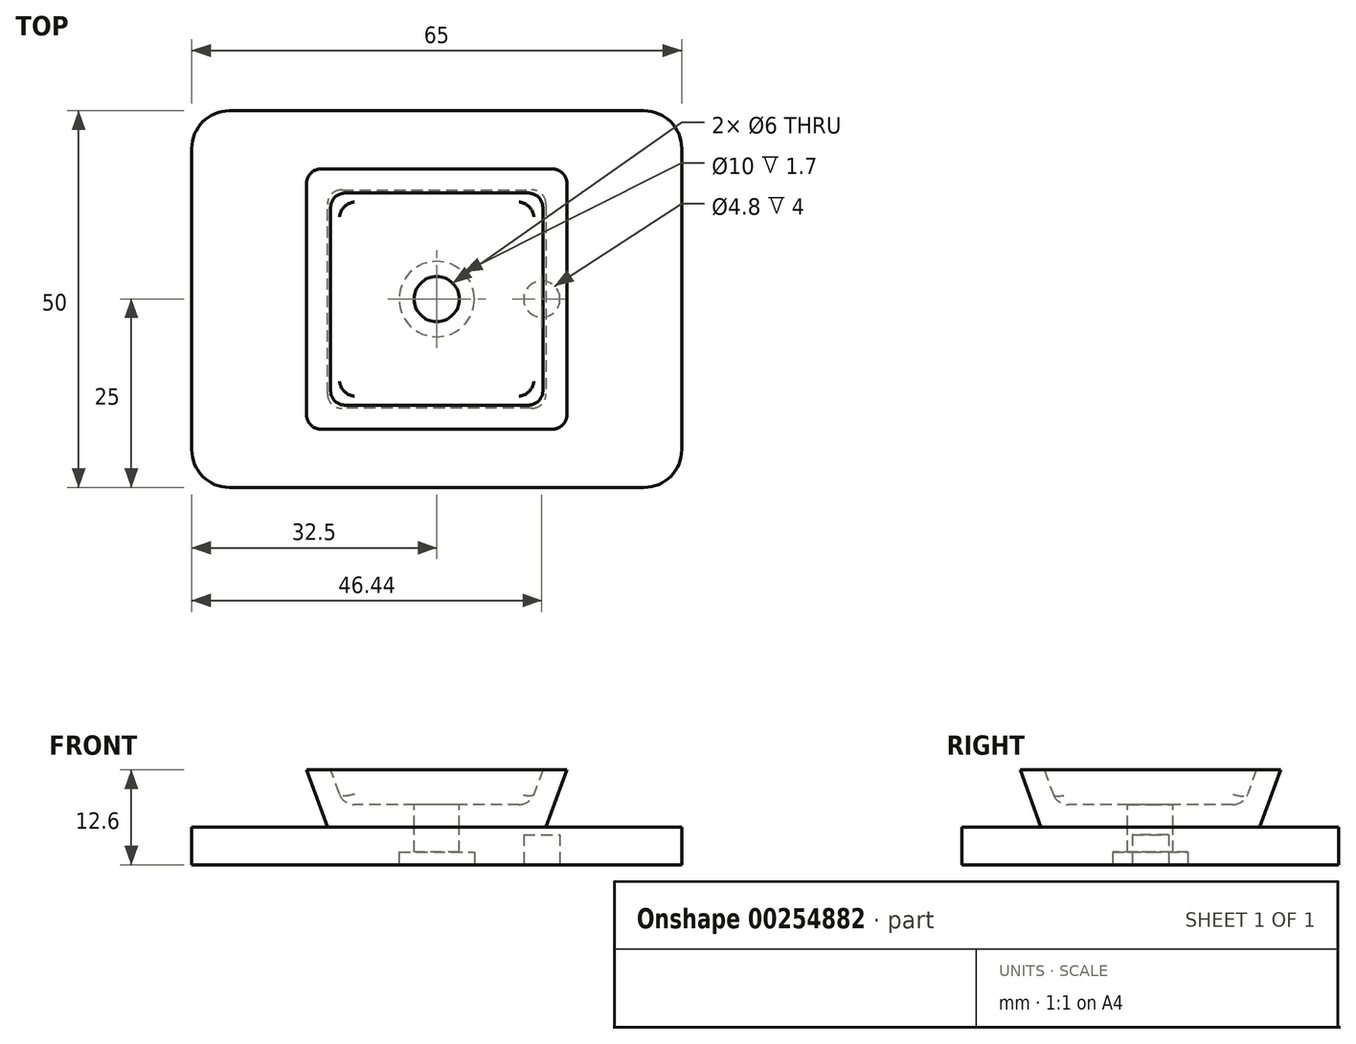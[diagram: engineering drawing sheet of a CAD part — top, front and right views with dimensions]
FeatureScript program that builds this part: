
annotation { "Feature Type Name" : "Feature", "Feature Type Description" : "" }
export const myFeature = defineFeature(function(context is Context, id is Id, definition is map)
    precondition{}
    {
        {
            var Q0;
            Q0=qCreatedBy(makeId("Top.planeOp"),FACE);
            var sketch = newSketch(context, id + "F0", { "sketchPlane" : qUnion([Q0])});
            skLineSegment(sketch, "E0.bottom", {"start": v(17.5, 17.5) * mm, "end": v(-17.5, 17.5) * mm});
            skLineSegment(sketch, "E0.top", {"start": v(17.5, -17.5) * mm, "end": v(-17.5, -17.5) * mm});
            skLineSegment(sketch, "E0.left", {"start": v(17.5, 17.5) * mm, "end": v(17.5, -17.5) * mm});
            skLineSegment(sketch, "E0.right", {"start": v(-17.5, 17.5) * mm, "end": v(-17.5, -17.5) * mm});
            skPoint(sketch, "E0.middle", {"position": v(0, 0) * mm});
            skSolve(sketch);
        }
        {
            var Q0;
            Q0=makeQuery(id+"F0.imprint","IMPRINT",FACE,{"disambiguationData":[TD([[makeQuery(id+"F0.imprint","IMPRINT",EDGE,{"derivedFrom":sQuery(id+"F0.wireOp",EDGE,"E0.bottom")}),1.0]])]});
            extrude(context, id + "F1", {"entities" : qUnion([Q0]), "depth" : 7.6 * mm});
        }
        {
            var Q0;
            Q0=makeQuery(id+"F1.opExtrude","CAP_EDGE",EDGE,{"disambiguationData":[OSD([sQuery(id+"F0.wireOp",EDGE,"E0.left")])],"isStart":true});
            var Q1;
            Q1=makeQuery(id+"F1.opExtrude","CAP_EDGE",EDGE,{"disambiguationData":[OSD([sQuery(id+"F0.wireOp",EDGE,"E0.top")])],"isStart":true});
            var Q2;
            Q2=makeQuery(id+"F1.opExtrude","CAP_EDGE",EDGE,{"disambiguationData":[OSD([sQuery(id+"F0.wireOp",EDGE,"E0.right")])],"isStart":true});
            var Q3;
            Q3=makeQuery(id+"F1.opExtrude","CAP_EDGE",EDGE,{"disambiguationData":[OSD([sQuery(id+"F0.wireOp",EDGE,"E0.bottom")])],"isStart":true});
            chamfer(context, id + "F2", {"entities" : qUnion([Q0, Q1, Q2, Q3]), "chamferType" : ChamferType.OFFSET_ANGLE, "width" : 3 * mm, "oppositeDirection" : false, "angle" : 70 * degree, "tangentPropagation" : true});
        }
        {
            var Q0;
            Q0=makeQuery(id+"F1.opExtrude","CAP_FACE",FACE,{"disambiguationData":[OSD([sQuery(id+"F0.wireOp",EDGE,"E0.bottom"),sQuery(id+"F0.wireOp",EDGE,"E0.top"),sQuery(id+"F0.wireOp",EDGE,"E0.left"),sQuery(id+"F0.wireOp",EDGE,"E0.right")])],"isStart":false});
            shell(context, id + "F3", {"entities" : qUnion([Q0]), "thickness" : 3 * mm});
        }
        {
            var Q0;
            Q0=makeQuery(id+"F3.opShell","OFFSET_FACE",FACE,{"disambiguationData":[OSD([sQuery(id+"F0.wireOp",EDGE,"E0.bottom"),sQuery(id+"F0.wireOp",EDGE,"E0.top"),sQuery(id+"F0.wireOp",EDGE,"E0.left"),sQuery(id+"F0.wireOp",EDGE,"E0.right")])]});
            var sketch = newSketch(context, id + "F4", { "sketchPlane" : qUnion([Q0])});
            skCircle(sketch, "E1", {"center": v(0, 0) * mm, "radius": 3 * mm});
            skSolve(sketch);
        }
        {
            var Q0;
            Q0 = qSketchRegion(id + "F4", true);
            extrude(context, id + "F5", {"entities" : qUnion([Q0]), "operationType" : NewBodyOperationType.REMOVE, "oppositeDirection" : true, "depth" : 25 * mm});
        }
        {
            var Q0;
            Q0=makeQuery(id+"F1.opExtrude","CAP_FACE",FACE,{"disambiguationData":[OSD([sQuery(id+"F0.wireOp",EDGE,"E0.bottom"),sQuery(id+"F0.wireOp",EDGE,"E0.top"),sQuery(id+"F0.wireOp",EDGE,"E0.left"),sQuery(id+"F0.wireOp",EDGE,"E0.right")])],"isStart":true});
            var sketch = newSketch(context, id + "F6", { "sketchPlane" : qUnion([Q0])});
            skLineSegment(sketch, "E2.bottom", {"start": v(32.5, -25) * mm, "end": v(-32.5, -25) * mm});
            skLineSegment(sketch, "E2.top", {"start": v(32.5, 25) * mm, "end": v(-32.5, 25) * mm});
            skLineSegment(sketch, "E2.left", {"start": v(32.5, -25) * mm, "end": v(32.5, 25) * mm});
            skLineSegment(sketch, "E2.right", {"start": v(-32.5, -25) * mm, "end": v(-32.5, 25) * mm});
            skPoint(sketch, "E2.middle", {"position": v(0, 0) * mm});
            skSolve(sketch);
        }
        {
            var Q0;
            Q0=makeQuery(id+"F6.imprint","IMPRINT",FACE,{"disambiguationData":[TD([[makeQuery(id+"F6.imprint","IMPRINT",EDGE,{"derivedFrom":sQuery(id+"F6.wireOp",EDGE,"E2.bottom")}),-1.0]])]});
            var Q1;
            {var subQ0=sQuery(id+"F0.wireOp",EDGE,"E0.right");var subQ1=sQuery(id+"F0.wireOp",EDGE,"E0.left");var subQ2=sQuery(id+"F0.wireOp",EDGE,"E0.top");var subQ3=sQuery(id+"F0.wireOp",EDGE,"E0.bottom");var subQ4=makeQuery(id+"F1.opExtrude","CAP_FACE",FACE,{"disambiguationData":[OSD([subQ3,subQ2,subQ1,subQ0])],"isStart":true});Q1=makeQuery(id+"F6.imprint","IMPRINT",FACE,{"disambiguationData":[TD([[makeQuery(id+"F6.imprint","IMPRINT",EDGE,{"derivedFrom":makeQuery(id+"F2.opChamfer","BLEND_EDGE",EDGE,{"blendedFrom":[makeQuery(id+"F1.opExtrude","CAP_EDGE",EDGE,{"disambiguationData":[OSD([subQ3])],"isStart":true}),subQ4],"blendedInto":[subQ4]})}),1.0]])]});}
            extrude(context, id + "F7", {"entities" : qUnion([Q0, Q1]), "depth" : 5 * mm});
        }
        {
            var Q0;
            Q0=makeQuery(id+"F7.opExtrude","CAP_FACE",FACE,{"disambiguationData":[OSD([sQuery(id+"F0.wireOp",EDGE,"E0.bottom"),sQuery(id+"F0.wireOp",EDGE,"E0.top"),sQuery(id+"F0.wireOp",EDGE,"E0.left"),sQuery(id+"F0.wireOp",EDGE,"E0.right"),sQuery(id+"F4.wireOp",EDGE,"E1"),sQuery(id+"F6.wireOp",EDGE,"E2.bottom"),sQuery(id+"F6.wireOp",EDGE,"E2.top"),sQuery(id+"F6.wireOp",EDGE,"E2.left"),sQuery(id+"F6.wireOp",EDGE,"E2.right")])],"isStart":false});
            var sketch = newSketch(context, id + "F8", { "sketchPlane" : qUnion([Q0])});
            skCircle(sketch, "E3", {"center": v(0, 0) * mm, "radius": 5 * mm});
            skSolve(sketch);
        }
        {
            var Q0;
            Q0=makeQuery(id+"F8.imprint","IMPRINT",FACE,{"disambiguationData":[TD([[makeQuery(id+"F8.imprint","IMPRINT",EDGE,{"derivedFrom":sQuery(id+"F8.wireOp",EDGE,"E3")}),1.0]])]});
            extrude(context, id + "F9", {"entities" : qUnion([Q0]), "operationType" : NewBodyOperationType.REMOVE, "oppositeDirection" : true, "depth" : 1.7 * mm});
        }
        {
            var Q0;
            Q0=makeQuery(id+"F7.opExtrude","CAP_FACE",FACE,{"disambiguationData":[OSD([sQuery(id+"F0.wireOp",EDGE,"E0.bottom"),sQuery(id+"F0.wireOp",EDGE,"E0.top"),sQuery(id+"F0.wireOp",EDGE,"E0.left"),sQuery(id+"F0.wireOp",EDGE,"E0.right"),sQuery(id+"F4.wireOp",EDGE,"E1"),sQuery(id+"F6.wireOp",EDGE,"E2.bottom"),sQuery(id+"F6.wireOp",EDGE,"E2.top"),sQuery(id+"F6.wireOp",EDGE,"E2.left"),sQuery(id+"F6.wireOp",EDGE,"E2.right")])],"isStart":false});
            var sketch = newSketch(context, id + "F10", { "sketchPlane" : qUnion([Q0])});
            skCircle(sketch, "E4", {"center": v(13.94, 0) * mm, "radius": 2.4 * mm});
            skSolve(sketch);
        }
        {
            var Q0;
            Q0=makeQuery(id+"F10.imprint","IMPRINT",FACE,{"disambiguationData":[TD([[makeQuery(id+"F10.imprint","IMPRINT",EDGE,{"derivedFrom":sQuery(id+"F10.wireOp",EDGE,"E4")}),1.0]])]});
            extrude(context, id + "F11", {"entities" : qUnion([Q0]), "operationType" : NewBodyOperationType.REMOVE, "oppositeDirection" : true, "depth" : 4 * mm});
        }
        {
            var Q0;
            Q0=makeQuery(id+"F2.opChamfer","BLEND_EDGE",EDGE,{"blendedFrom":[makeQuery(id+"F1.opExtrude","CAP_EDGE",EDGE,{"disambiguationData":[OSD([sQuery(id+"F0.wireOp",EDGE,"E0.top")])],"isStart":true}),makeQuery(id+"F1.opExtrude","CAP_EDGE",EDGE,{"disambiguationData":[OSD([sQuery(id+"F0.wireOp",EDGE,"E0.right")])],"isStart":true})],"blendedInto":[]});
            var Q1;
            Q1=makeQuery(id+"F2.opChamfer","BLEND_EDGE",EDGE,{"blendedFrom":[makeQuery(id+"F1.opExtrude","CAP_EDGE",EDGE,{"disambiguationData":[OSD([sQuery(id+"F0.wireOp",EDGE,"E0.top")])],"isStart":true}),makeQuery(id+"F1.opExtrude","CAP_EDGE",EDGE,{"disambiguationData":[OSD([sQuery(id+"F0.wireOp",EDGE,"E0.left")])],"isStart":true})],"blendedInto":[]});
            var Q2;
            Q2=makeQuery(id+"F2.opChamfer","BLEND_EDGE",EDGE,{"blendedFrom":[makeQuery(id+"F1.opExtrude","CAP_EDGE",EDGE,{"disambiguationData":[OSD([sQuery(id+"F0.wireOp",EDGE,"E0.bottom")])],"isStart":true}),makeQuery(id+"F1.opExtrude","CAP_EDGE",EDGE,{"disambiguationData":[OSD([sQuery(id+"F0.wireOp",EDGE,"E0.left")])],"isStart":true})],"blendedInto":[]});
            var Q3;
            Q3=makeQuery(id+"F2.opChamfer","BLEND_EDGE",EDGE,{"blendedFrom":[makeQuery(id+"F1.opExtrude","CAP_EDGE",EDGE,{"disambiguationData":[OSD([sQuery(id+"F0.wireOp",EDGE,"E0.bottom")])],"isStart":true}),makeQuery(id+"F1.opExtrude","CAP_EDGE",EDGE,{"disambiguationData":[OSD([sQuery(id+"F0.wireOp",EDGE,"E0.right")])],"isStart":true})],"blendedInto":[]});
            var Q4;
            Q4=makeQuery(id+"F3.opShell","OFFSET_EDGE",EDGE,{"disambiguationData":[OSD([sQuery(id+"F0.wireOp",EDGE,"E0.bottom"),sQuery(id+"F0.wireOp",EDGE,"E0.left")])]});
            var Q5;
            Q5=makeQuery(id+"F3.opShell","OFFSET_EDGE",EDGE,{"disambiguationData":[OSD([sQuery(id+"F0.wireOp",EDGE,"E0.bottom"),sQuery(id+"F0.wireOp",EDGE,"E0.right")])]});
            var Q6;
            {var subQ0=sQuery(id+"F0.wireOp",EDGE,"E0.right");var subQ1=sQuery(id+"F0.wireOp",EDGE,"E0.left");var subQ2=sQuery(id+"F0.wireOp",EDGE,"E0.top");var subQ3=sQuery(id+"F0.wireOp",EDGE,"E0.bottom");Q6=makeQuery(id+"F3.opShell","OFFSET_EDGE",EDGE,{"disambiguationData":[OSD([subQ3,subQ2,subQ1,subQ0]),TDD([makeQuery(id+"F2.opChamfer","BLEND_EDGE",EDGE,{"blendedFrom":[makeQuery(id+"F1.opExtrude","CAP_EDGE",EDGE,{"disambiguationData":[OSD([subQ3])],"isStart":true}),makeQuery(id+"F1.opExtrude","CAP_FACE",FACE,{"disambiguationData":[OSD([subQ3,subQ2,subQ1,subQ0])],"isStart":true})],"blendedInto":[makeQuery(id+"F1.opExtrude","CAP_FACE",FACE,{"disambiguationData":[OSD([subQ3,subQ2,subQ1,subQ0])],"isStart":true})]})])]});}
            var Q7;
            {var subQ0=sQuery(id+"F0.wireOp",EDGE,"E0.right");var subQ1=sQuery(id+"F0.wireOp",EDGE,"E0.left");var subQ2=sQuery(id+"F0.wireOp",EDGE,"E0.top");var subQ3=sQuery(id+"F0.wireOp",EDGE,"E0.bottom");Q7=makeQuery(id+"F3.opShell","OFFSET_EDGE",EDGE,{"disambiguationData":[OSD([subQ3,subQ2,subQ1,subQ0]),TDD([makeQuery(id+"F2.opChamfer","BLEND_EDGE",EDGE,{"blendedFrom":[makeQuery(id+"F1.opExtrude","CAP_EDGE",EDGE,{"disambiguationData":[OSD([subQ1])],"isStart":true}),makeQuery(id+"F1.opExtrude","CAP_FACE",FACE,{"disambiguationData":[OSD([subQ3,subQ2,subQ1,subQ0])],"isStart":true})],"blendedInto":[makeQuery(id+"F1.opExtrude","CAP_FACE",FACE,{"disambiguationData":[OSD([subQ3,subQ2,subQ1,subQ0])],"isStart":true})]})])]});}
            var Q8;
            {var subQ0=sQuery(id+"F0.wireOp",EDGE,"E0.right");var subQ1=sQuery(id+"F0.wireOp",EDGE,"E0.left");var subQ2=sQuery(id+"F0.wireOp",EDGE,"E0.top");var subQ3=sQuery(id+"F0.wireOp",EDGE,"E0.bottom");Q8=makeQuery(id+"F3.opShell","OFFSET_EDGE",EDGE,{"disambiguationData":[OSD([subQ3,subQ2,subQ1,subQ0]),TDD([makeQuery(id+"F2.opChamfer","BLEND_EDGE",EDGE,{"blendedFrom":[makeQuery(id+"F1.opExtrude","CAP_EDGE",EDGE,{"disambiguationData":[OSD([subQ0])],"isStart":true}),makeQuery(id+"F1.opExtrude","CAP_FACE",FACE,{"disambiguationData":[OSD([subQ3,subQ2,subQ1,subQ0])],"isStart":true})],"blendedInto":[makeQuery(id+"F1.opExtrude","CAP_FACE",FACE,{"disambiguationData":[OSD([subQ3,subQ2,subQ1,subQ0])],"isStart":true})]})])]});}
            var Q9;
            {var subQ0=sQuery(id+"F0.wireOp",EDGE,"E0.right");var subQ1=sQuery(id+"F0.wireOp",EDGE,"E0.left");var subQ2=sQuery(id+"F0.wireOp",EDGE,"E0.top");var subQ3=sQuery(id+"F0.wireOp",EDGE,"E0.bottom");Q9=makeQuery(id+"F3.opShell","OFFSET_EDGE",EDGE,{"disambiguationData":[OSD([subQ3,subQ2,subQ1,subQ0]),TDD([makeQuery(id+"F2.opChamfer","BLEND_EDGE",EDGE,{"blendedFrom":[makeQuery(id+"F1.opExtrude","CAP_EDGE",EDGE,{"disambiguationData":[OSD([subQ2])],"isStart":true}),makeQuery(id+"F1.opExtrude","CAP_FACE",FACE,{"disambiguationData":[OSD([subQ3,subQ2,subQ1,subQ0])],"isStart":true})],"blendedInto":[makeQuery(id+"F1.opExtrude","CAP_FACE",FACE,{"disambiguationData":[OSD([subQ3,subQ2,subQ1,subQ0])],"isStart":true})]})])]});}
            var Q10;
            Q10=makeQuery(id+"F3.opShell","OFFSET_EDGE",EDGE,{"disambiguationData":[OSD([sQuery(id+"F0.wireOp",EDGE,"E0.top"),sQuery(id+"F0.wireOp",EDGE,"E0.left")])]});
            var Q11;
            Q11=makeQuery(id+"F3.opShell","OFFSET_EDGE",EDGE,{"disambiguationData":[OSD([sQuery(id+"F0.wireOp",EDGE,"E0.top"),sQuery(id+"F0.wireOp",EDGE,"E0.right")])]});
            fillet(context, id + "F12", {"entities" : qUnion([Q0, Q1, Q2, Q3, Q4, Q5, Q6, Q7, Q8, Q9, Q10, Q11]), "radius" : 2.07 * mm, "tangentPropagation" : true, "allowEdgeOverflow" : false});
        }
        {
            var Q0;
            Q0=makeQuery(id+"F7.opExtrude","SWEPT_EDGE",EDGE,{"disambiguationData":[OSD([sQuery(id+"F6.wireOp",EDGE,"E2.bottom"),sQuery(id+"F6.wireOp",EDGE,"E2.left")])]});
            var Q1;
            Q1=makeQuery(id+"F7.opExtrude","SWEPT_EDGE",EDGE,{"disambiguationData":[OSD([sQuery(id+"F6.wireOp",EDGE,"E2.top"),sQuery(id+"F6.wireOp",EDGE,"E2.left")])]});
            var Q2;
            Q2=makeQuery(id+"F7.opExtrude","SWEPT_EDGE",EDGE,{"disambiguationData":[OSD([sQuery(id+"F6.wireOp",EDGE,"E2.top"),sQuery(id+"F6.wireOp",EDGE,"E2.right")])]});
            var Q3;
            Q3=makeQuery(id+"F7.opExtrude","SWEPT_EDGE",EDGE,{"disambiguationData":[OSD([sQuery(id+"F6.wireOp",EDGE,"E2.bottom"),sQuery(id+"F6.wireOp",EDGE,"E2.right")])]});
            fillet(context, id + "F13", {"entities" : qUnion([Q0, Q1, Q2, Q3]), "radius" : 5 * mm, "tangentPropagation" : true, "allowEdgeOverflow" : false});
        }
    });
